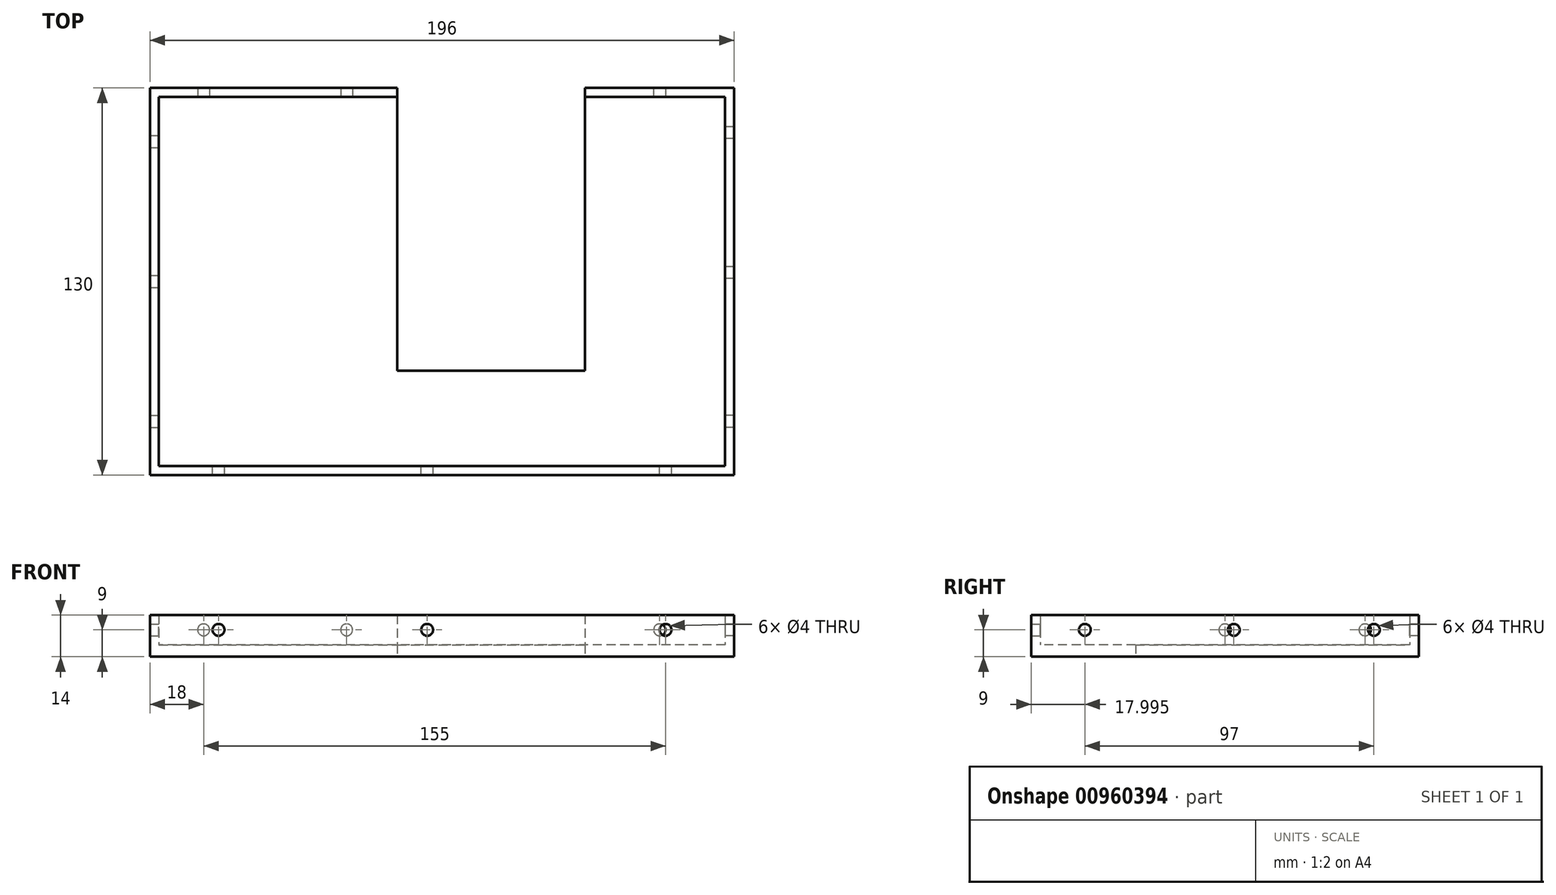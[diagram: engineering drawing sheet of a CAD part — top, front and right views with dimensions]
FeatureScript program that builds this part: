
annotation { "Feature Type Name" : "Feature", "Feature Type Description" : "" }
export const myFeature = defineFeature(function(context is Context, id is Id, definition is map)
    precondition{}
    {
        {
            var Q0;
            Q0=qCreatedBy(makeId("Top.planeOp"),FACE);
            var sketch = newSketch(context, id + "F0", { "sketchPlane" : qUnion([Q0])});
            skLineSegment(sketch, "E0.bottom", {"start": v(-97.73, 41) * mm, "end": v(-14.73, 41) * mm});
            skLineSegment(sketch, "E0.top", {"start": v(-97.73, -89) * mm, "end": v(98.27, -89) * mm});
            skLineSegment(sketch, "E0.left", {"start": v(-97.73, 41) * mm, "end": v(-97.73, -89) * mm});
            skLineSegment(sketch, "E0.right", {"start": v(98.27, 41) * mm, "end": v(98.27, -89) * mm});
            skLineSegment(sketch, "E1", {"start": v(-14.73, 41) * mm, "end": v(-14.73, -54) * mm});
            skLineSegment(sketch, "E2", {"start": v(-14.73, -54) * mm, "end": v(48.27, -54) * mm});
            skLineSegment(sketch, "E3", {"start": v(48.27, -54) * mm, "end": v(48.27, 41) * mm});
            skLineSegment(sketch, "E4.trimOffspring", {"start": v(48.27, 41) * mm, "end": v(98.27, 41) * mm});
            skSolve(sketch);
        }
        {
            var Q0;
            Q0 = qSketchRegion(id + "F0", true);
            extrude(context, id + "F1", {"entities" : qUnion([Q0]), "depth" : 4 * mm, "offsetDistance" : 25 * mm});
        }
        {
            var Q0;
            Q0=makeQuery(id+"F1.opExtrude","CAP_FACE",FACE,{"disambiguationData":[OSD([sQuery(id+"F0.wireOp",EDGE,"E0.bottom"),sQuery(id+"F0.wireOp",EDGE,"E0.top"),sQuery(id+"F0.wireOp",EDGE,"E0.left"),sQuery(id+"F0.wireOp",EDGE,"E0.right"),sQuery(id+"F0.wireOp",EDGE,"E1"),sQuery(id+"F0.wireOp",EDGE,"E2"),sQuery(id+"F0.wireOp",EDGE,"E3"),sQuery(id+"F0.wireOp",EDGE,"E4.trimOffspring")])],"isStart":false});
            var sketch = newSketch(context, id + "F2", { "sketchPlane" : qUnion([Q0])});
            skLineSegment(sketch, "E5", {"start": v(-94.73, 38) * mm, "end": v(-94.73, -86) * mm});
            skLineSegment(sketch, "E6", {"start": v(-94.73, 38) * mm, "end": v(-14.73, 38) * mm});
            skLineSegment(sketch, "E7", {"start": v(-97.73, -89) * mm, "end": v(-97.73, 41) * mm});
            skLineSegment(sketch, "E8", {"start": v(-97.73, 41) * mm, "end": v(-14.73, 41) * mm});
            skLineSegment(sketch, "E9", {"start": v(-14.73, 41) * mm, "end": v(-14.73, 38) * mm});
            skLineSegment(sketch, "E10", {"start": v(48.27, 41) * mm, "end": v(98.27, 41) * mm});
            skLineSegment(sketch, "E11", {"start": v(95.27, 38) * mm, "end": v(48.27, 38) * mm});
            skLineSegment(sketch, "E12", {"start": v(95.27, 38) * mm, "end": v(95.27, -86) * mm});
            skLineSegment(sketch, "E13", {"start": v(95.27, -86) * mm, "end": v(-94.73, -86) * mm});
            skLineSegment(sketch, "E14", {"start": v(98.27, 41) * mm, "end": v(98.27, -89) * mm});
            skLineSegment(sketch, "E15", {"start": v(98.27, -89) * mm, "end": v(-97.73, -89) * mm});
            skSolve(sketch);
        }
        {
            var Q0;
            Q0=makeQuery(id+"F2.imprint","IMPRINT",FACE,{"disambiguationData":[TD([[makeQuery(id+"F2.imprint","IMPRINT",EDGE,{"derivedFrom":sQuery(id+"F2.wireOp",EDGE,"E5")}),-1.0]])]});
            extrude(context, id + "F3", {"entities" : qUnion([Q0]), "operationType" : NewBodyOperationType.ADD, "depth" : 10 * mm, "offsetDistance" : 25 * mm});
        }
        {
            var Q0;
            Q0=makeQuery(id+"F3.opExtrude","SWEPT_FACE",FACE,{"disambiguationData":[OSD([sQuery(id+"F2.wireOp",EDGE,"E5")])]});
            var sketch = newSketch(context, id + "F4", { "sketchPlane" : qUnion([Q0])});
            skCircle(sketch, "E16", {"center": v(23, 9) * mm, "radius": 2 * mm});
            skCircle(sketch, "E17", {"center": v(-24, 9) * mm, "radius": 2 * mm});
            skPoint(sketch, "E17.centerSnap0", {"position": v(-24, 14) * mm});
            skCircle(sketch, "E18", {"center": v(-71, 9) * mm, "radius": 2 * mm});
            skSolve(sketch);
        }
        {
            var Q0;
            Q0 = qSketchRegion(id + "F4", true);
            extrude(context, id + "F5", {"entities" : qUnion([Q0]), "operationType" : NewBodyOperationType.REMOVE, "oppositeDirection" : true, "depth" : 5 * mm, "offsetDistance" : 25 * mm});
        }
        {
            var Q0;
            Q0=makeQuery(id+"F3.opExtrude","SWEPT_FACE",FACE,{"disambiguationData":[OSD([sQuery(id+"F2.wireOp",EDGE,"E6")])]});
            var sketch = newSketch(context, id + "F6", { "sketchPlane" : qUnion([Q0])});
            skCircle(sketch, "E19", {"center": v(-79.73, 9) * mm, "radius": 2 * mm});
            skPoint(sketch, "E19.centerSnap0", {"position": v(-94.73, 9) * mm});
            skCircle(sketch, "E20", {"center": v(-31.73, 9) * mm, "radius": 2 * mm});
            skCircle(sketch, "E21", {"center": v(73.27, 9) * mm, "radius": 2 * mm});
            skSolve(sketch);
        }
        {
            var Q0;
            Q0=makeQuery(id+"F3.opExtrude","SWEPT_FACE",FACE,{"disambiguationData":[OSD([sQuery(id+"F2.wireOp",EDGE,"E12")])]});
            var sketch = newSketch(context, id + "F7", { "sketchPlane" : qUnion([Q0])});
            skCircle(sketch, "E22", {"center": v(71, 9) * mm, "radius": 2 * mm});
            skCircle(sketch, "E23", {"center": v(21, 9) * mm, "radius": 2 * mm});
            skPoint(sketch, "E23.centerSnap0", {"position": v(21, 14) * mm});
            skCircle(sketch, "E24", {"center": v(-26, 9) * mm, "radius": 2 * mm});
            skSolve(sketch);
        }
        {
            var Q0;
            Q0 = qSketchRegion(id + "F7", true);
            extrude(context, id + "F8", {"entities" : qUnion([Q0]), "operationType" : NewBodyOperationType.REMOVE, "oppositeDirection" : true, "depth" : 5 * mm, "offsetDistance" : 25 * mm});
        }
        {
            var Q0;
            Q0 = qSketchRegion(id + "F6", true);
            extrude(context, id + "F9", {"entities" : qUnion([Q0]), "operationType" : NewBodyOperationType.REMOVE, "oppositeDirection" : true, "depth" : 5 * mm, "offsetDistance" : 25 * mm});
        }
        {
            var Q0;
            Q0=makeQuery(id+"F3.opExtrude","SWEPT_FACE",FACE,{"disambiguationData":[OSD([sQuery(id+"F2.wireOp",EDGE,"E13")])]});
            var sketch = newSketch(context, id + "F10", { "sketchPlane" : qUnion([Q0])});
            skCircle(sketch, "E25", {"center": v(-75.27, 9) * mm, "radius": 2 * mm});
            skCircle(sketch, "E26", {"center": v(4.73, 9) * mm, "radius": 2 * mm});
            skCircle(sketch, "E27", {"center": v(74.73, 9) * mm, "radius": 2 * mm});
            skSolve(sketch);
        }
        {
            var Q0;
            Q0 = qSketchRegion(id + "F10", true);
            extrude(context, id + "F11", {"entities" : qUnion([Q0]), "operationType" : NewBodyOperationType.REMOVE, "oppositeDirection" : true, "depth" : 5 * mm, "offsetDistance" : 25 * mm});
        }
    });
